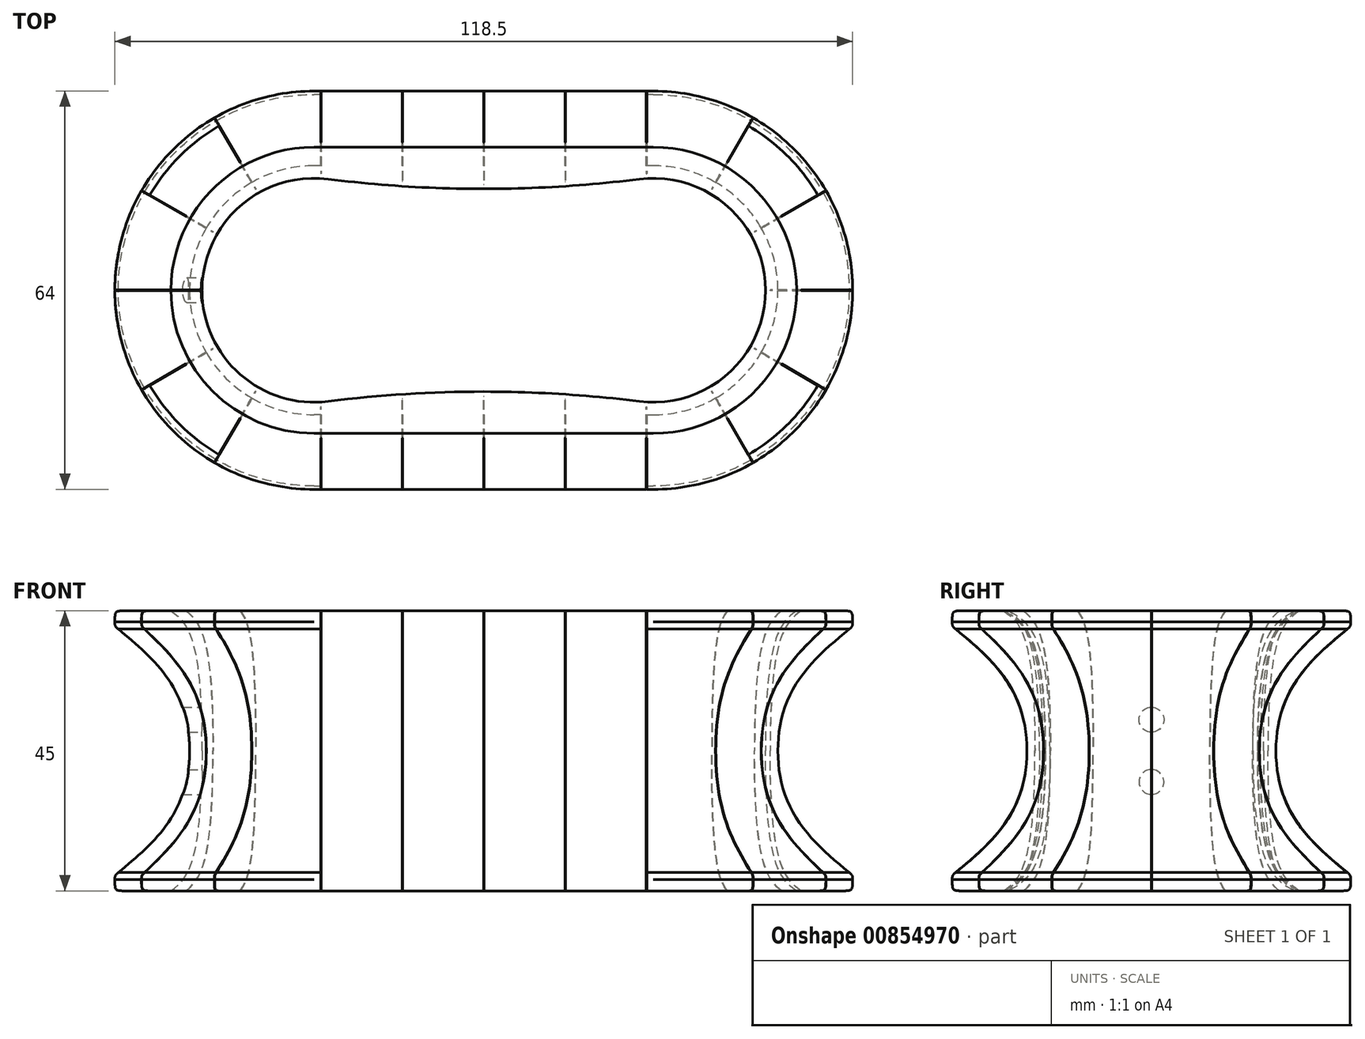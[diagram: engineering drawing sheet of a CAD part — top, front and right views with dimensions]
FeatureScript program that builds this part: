
annotation { "Feature Type Name" : "Feature", "Feature Type Description" : "" }
export const myFeature = defineFeature(function(context is Context, id is Id, definition is map)
    precondition{}
    {
        {
            var Q0;
            Q0=qCreatedBy(makeId("Top.planeOp"),FACE);
            var sketch = newSketch(context, id + "F0", { "sketchPlane" : qUnion([Q0])});
            skArc(sketch, "E0", {"start": v(-25, 17.86) * mm, "mid": v(0, 16.3) * mm, "end": v(25, 17.86) * mm});
            skArc(sketch, "E1", {"start": v(25, -17.86) * mm, "mid": v(45.25, 0) * mm, "end": v(25, 17.86) * mm});
            skArc(sketch, "E2", {"start": v(-25, 17.86) * mm, "mid": v(-45.25, 0) * mm, "end": v(-25, -17.86) * mm});
            skArc(sketch, "E3", {"start": v(25, -17.86) * mm, "mid": v(0, -16.3) * mm, "end": v(-25, -17.86) * mm});
            skLineSegment(sketch, "E4", {"start": v(-27.25, 0) * mm, "end": v(27.25, 0) * mm, "construction": true});
            skSolve(sketch);
        }
        {
            var Q0;
            Q0=qCreatedBy(makeId("Top.planeOp"),FACE);
            cPlane(context, id + "F1", {"entities" : qUnion([Q0]), "cplaneType" : CPlaneType.OFFSET, "offset" : 20 * mm, "width" : 150 * mm, "height" : 150 * mm});
        }
        {
            var Q0;
            Q0=qCreatedBy(makeId("Top.planeOp"),FACE);
            var sketch = newSketch(context, id + "F2", { "sketchPlane" : qUnion([Q0])});
            skArc(sketch, "E5", {"start": v(-27.25, 20) * mm, "mid": v(-47.25, 0) * mm, "end": v(-27.25, -20) * mm});
            skArc(sketch, "E6", {"start": v(27.25, -20) * mm, "mid": v(47.25, 0) * mm, "end": v(27.25, 20) * mm});
            skLineSegment(sketch, "E7", {"start": v(-27.25, 20) * mm, "end": v(27.25, 20) * mm});
            skLineSegment(sketch, "E8", {"start": v(27.25, -20) * mm, "end": v(-27.25, -20) * mm});
            skSolve(sketch);
        }
        {
            var Q0;
            Q0=qCreatedBy(id+"F1.planeOp",FACE);
            var sketch = newSketch(context, id + "F3", { "sketchPlane" : qUnion([Q0])});
            skLineSegment(sketch, "E9.0", {"start": v(-27.25, 32) * mm, "end": v(27.25, 32) * mm});
            skArc(sketch, "E9.1", {"start": v(-27.25, 32) * mm, "mid": v(-59.25, 0) * mm, "end": v(-27.25, -32) * mm});
            skLineSegment(sketch, "E9.2", {"start": v(27.25, -32) * mm, "end": v(-27.25, -32) * mm});
            skArc(sketch, "E9.3", {"start": v(27.25, -32) * mm, "mid": v(59.25, 0) * mm, "end": v(27.25, 32) * mm});
            skSolve(sketch);
        }
        {
            var Q0;
            Q0=makeQuery(id+"F2.imprint","IMPRINT",FACE,{"disambiguationData":[TD([[makeQuery(id+"F2.imprint","IMPRINT",EDGE,{"derivedFrom":sQuery(id+"F2.wireOp",EDGE,"E5")}),1.0]])]});
            var Q1;
            Q1=makeQuery(id+"F3.imprint","IMPRINT",FACE,{"disambiguationData":[TD([[makeQuery(id+"F3.imprint","IMPRINT",EDGE,{"derivedFrom":sQuery(id+"F3.wireOp",EDGE,"E9.0")}),-1.0]])]});
            loft(context, id + "F4", {"startCondition" : LoftEndDerivativeType.NORMAL_TO_PROFILE, "startMagnitude" : 1.5, "sheetProfilesArray" : [{ "sheetProfileEntities" : qUnion([Q0]) }, { "sheetProfileEntities" : qUnion([Q1]) }]});
        }
        {
            var Q0;
            Q0=makeQuery(id+"F4.opLoft","CAP_FACE",FACE,{"disambiguationData":[OSD([makeQuery(id+"F3.imprint","IMPRINT",FACE,{"disambiguationData":[TD([[makeQuery(id+"F3.imprint","IMPRINT",EDGE,{"derivedFrom":sQuery(id+"F3.wireOp",EDGE,"E9.0")}),-1.0]])]})])],"isStart":true});
            extrude(context, id + "F5", {"entities" : qUnion([Q0]), "operationType" : NewBodyOperationType.ADD, "depth" : 2.5 * mm, "offsetDistance" : 25 * mm});
        }
        {
            var Q0;
            Q0=makeQuery(id+"F5.opExtrude","CAP_FACE",FACE,{"disambiguationData":[OSD([makeQuery(id+"F3.imprint","IMPRINT",FACE,{"disambiguationData":[TD([[makeQuery(id+"F3.imprint","IMPRINT",EDGE,{"derivedFrom":sQuery(id+"F3.wireOp",EDGE,"E9.0")}),-1.0]])]})])],"isStart":false});
            var sketch = newSketch(context, id + "F6", { "sketchPlane" : qUnion([Q0])});
            skArc(sketch, "E10", {"start": v(-27.25, 23) * mm, "mid": v(-50.25, 0) * mm, "end": v(-27.25, -23) * mm});
            skArc(sketch, "E11", {"start": v(27.25, -23) * mm, "mid": v(50.25, 0) * mm, "end": v(27.25, 23) * mm});
            skLineSegment(sketch, "E12", {"start": v(-27.25, 23) * mm, "end": v(27.25, 23) * mm});
            skLineSegment(sketch, "E13", {"start": v(27.25, -23) * mm, "end": v(-27.25, -23) * mm});
            skSolve(sketch);
        }
        {
            var Q1;
            Q1=makeQuery(id+"F6.imprint","IMPRINT",FACE,{"disambiguationData":[TD([[makeQuery(id+"F6.imprint","IMPRINT",EDGE,{"derivedFrom":sQuery(id+"F6.wireOp",EDGE,"E10")}),1.0]])]});
            var Q2;
            Q2=makeQuery(id+"F0.imprint","IMPRINT",FACE,{"disambiguationData":[TD([[makeQuery(id+"F0.imprint","IMPRINT",EDGE,{"derivedFrom":sQuery(id+"F0.wireOp",EDGE,"E0")}),-1.0]])]});
            loft(context, id + "F7", {"operationType" : NewBodyOperationType.REMOVE, "endCondition" : LoftEndDerivativeType.NORMAL_TO_PROFILE, "endMagnitude" : 2.5, "sheetProfilesArray" : [{ "sheetProfileEntities" : qUnion([Q1]) }, { "sheetProfileEntities" : qUnion([Q2]) }]});
        }
        {
            var Q0;
            Q0=qCreatedBy(makeId("Top.planeOp"),FACE);
            var sketch = newSketch(context, id + "F8", { "sketchPlane" : qUnion([Q0])});
            skLineSegment(sketch, "E14", {"start": v(-65.05, 0) * mm, "end": v(-65.05, -15.33) * mm, "construction": true});
            skLineSegment(sketch, "E15", {"start": v(-65.05, -15.33) * mm, "end": v(-56.29, -30.51) * mm, "construction": true});
            skLineSegment(sketch, "E16", {"start": v(-56.29, -30.51) * mm, "end": v(-41.1, -39.28) * mm, "construction": true});
            skLineSegment(sketch, "E17", {"start": v(-41.1, -39.28) * mm, "end": v(22.99, -39.28) * mm, "construction": true});
            skSolve(sketch);
        }
        {
            var Q0;
            {var subQ0=sQuery(id+"F3.wireOp",EDGE,"E9.2");var subQ1=sQuery(id+"F3.wireOp",EDGE,"E9.1");var subQ2=sQuery(id+"F3.wireOp",EDGE,"E9.0");Q0=makeQuery(id+"F5.boolean.opBoolean","MERGE",EDGE,{"derivedFrom":[makeQuery(id+"F4.opLoft","MID_CAP_EDGE",EDGE,{"disambiguationData":[OSD([subQ2,subQ1,subQ0])],"capPos":1.0}),makeQuery(id+"F5.opExtrude","CAP_EDGE",EDGE,{"disambiguationData":[OSD([subQ2,subQ1,subQ0])],"isStart":true})]});}
            var Q1;
            Q1=makeQuery(id+"F5.opExtrude","CAP_EDGE",EDGE,{"disambiguationData":[OSD([sQuery(id+"F3.wireOp",EDGE,"E9.0"),sQuery(id+"F3.wireOp",EDGE,"E9.1"),sQuery(id+"F3.wireOp",EDGE,"E9.2")])],"isStart":false});
            fillet(context, id + "F9", {"entities" : qUnion([Q0, Q1]), "radius" : 1.5 * mm, "tangentPropagation" : true, "rho" : .7, "crossSection" : FilletCrossSection.CONIC, "allowEdgeOverflow" : false});
        }
        {
            var Q0;
            Q0=sQuery(id+"F8.wireOp",EDGE,"E14");
            cPlane(context, id + "F10", {"entities" : qUnion([Q0]), "cplaneType" : CPlaneType.LINE_ANGLE, "offset" : 25 * mm, "angle" : 90 * degree, "width" : 150 * mm, "height" : 150 * mm});
        }
        {
            var Q0;
            Q0=sQuery(id+"F8.wireOp",EDGE,"E15");
            cPlane(context, id + "F11", {"entities" : qUnion([Q0]), "cplaneType" : CPlaneType.LINE_ANGLE, "offset" : 25 * mm, "angle" : 90 * degree, "width" : 150 * mm, "height" : 150 * mm});
        }
        {
            var Q0;
            Q0=sQuery(id+"F8.wireOp",EDGE,"E16");
            cPlane(context, id + "F12", {"entities" : qUnion([Q0]), "cplaneType" : CPlaneType.LINE_ANGLE, "offset" : 90 * mm, "angle" : 0 * degree, "width" : 150 * mm, "height" : 150 * mm});
        }
        {
            var Q0;
            Q0=sQuery(id+"F8.wireOp",EDGE,"E17");
            cPlane(context, id + "F13", {"entities" : qUnion([Q0]), "cplaneType" : CPlaneType.LINE_ANGLE, "offset" : 25 * mm, "angle" : 0 * degree, "oppositeDirection" : true, "width" : 150 * mm, "height" : 150 * mm});
        }
        {
            var Q0;
            Q0=qCreatedBy(id+"F10.planeOp",FACE);
            var sketch = newSketch(context, id + "F14", { "sketchPlane" : qUnion([Q0])});
            skLineSegment(sketch, "E18.bottom", {"start": v(0.04, 0) * mm, "end": v(-0.04, 0) * mm});
            skLineSegment(sketch, "E18.top", {"start": v(0.04, 22.5) * mm, "end": v(-0.04, 22.5) * mm});
            skLineSegment(sketch, "E18.left", {"start": v(0.04, 0) * mm, "end": v(0.04, 22.5) * mm});
            skLineSegment(sketch, "E18.right", {"start": v(-0.04, 0) * mm, "end": v(-0.04, 22.5) * mm});
            skSolve(sketch);
        }
        {
            var Q0;
            Q0=qCreatedBy(id+"F11.planeOp",FACE);
            var sketch = newSketch(context, id + "F15", { "sketchPlane" : qUnion([Q0])});
            skLineSegment(sketch, "E19.bottom", {"start": v(13.66, 0) * mm, "end": v(13.59, 0) * mm});
            skLineSegment(sketch, "E19.top", {"start": v(13.66, 22.5) * mm, "end": v(13.59, 22.5) * mm});
            skLineSegment(sketch, "E19.left", {"start": v(13.66, 0) * mm, "end": v(13.66, 22.5) * mm});
            skLineSegment(sketch, "E19.right", {"start": v(13.59, 0) * mm, "end": v(13.59, 22.5) * mm});
            skSolve(sketch);
        }
        {
            var Q0;
            Q0=qCreatedBy(id+"F12.planeOp",FACE);
            var sketch = newSketch(context, id + "F16", { "sketchPlane" : qUnion([Q0])});
            skLineSegment(sketch, "E20.bottom", {"start": v(23.64, 0) * mm, "end": v(23.56, 0) * mm});
            skLineSegment(sketch, "E20.top", {"start": v(23.64, 22.5) * mm, "end": v(23.56, 22.5) * mm});
            skLineSegment(sketch, "E20.left", {"start": v(23.56, 0) * mm, "end": v(23.56, 22.5) * mm});
            skLineSegment(sketch, "E20.right", {"start": v(23.64, 0) * mm, "end": v(23.64, 22.5) * mm});
            skSolve(sketch);
        }
        {
            var Q0;
            Q0=qCreatedBy(id+"F13.planeOp",FACE);
            var sketch = newSketch(context, id + "F17", { "sketchPlane" : qUnion([Q0])});
            skLineSegment(sketch, "E21.bottom", {"start": v(0.04, 0) * mm, "end": v(-0.04, 0) * mm});
            skLineSegment(sketch, "E21.top", {"start": v(0.04, 22.5) * mm, "end": v(-0.04, 22.5) * mm});
            skLineSegment(sketch, "E21.left", {"start": v(0.04, 0) * mm, "end": v(0.04, 22.5) * mm});
            skLineSegment(sketch, "E21.right", {"start": v(-0.04, 0) * mm, "end": v(-0.04, 22.5) * mm});
            skLineSegment(sketch, "E22.bottom", {"start": v(13.04, 0) * mm, "end": v(13.11, 0) * mm});
            skLineSegment(sketch, "E22.top", {"start": v(13.04, 22.5) * mm, "end": v(13.11, 22.5) * mm});
            skLineSegment(sketch, "E22.left", {"start": v(13.04, 0) * mm, "end": v(13.04, 22.5) * mm});
            skLineSegment(sketch, "E22.right", {"start": v(13.11, 0) * mm, "end": v(13.11, 22.5) * mm});
            skLineSegment(sketch, "E23.bottom", {"start": v(26.11, 0) * mm, "end": v(26.19, 0) * mm});
            skLineSegment(sketch, "E23.top", {"start": v(26.11, 22.5) * mm, "end": v(26.19, 22.5) * mm});
            skLineSegment(sketch, "E23.left", {"start": v(26.11, 0) * mm, "end": v(26.11, 22.5) * mm});
            skLineSegment(sketch, "E23.right", {"start": v(26.19, 0) * mm, "end": v(26.19, 22.5) * mm});
            skLineSegment(sketch, "E24", {"start": v(26.11, 11.25) * mm, "end": v(13.11, 11.25) * mm, "construction": true});
            skLineSegment(sketch, "E25", {"start": v(13.04, 11.25) * mm, "end": v(0.04, 11.25) * mm, "construction": true});
            skSolve(sketch);
        }
        {
            var Q0;
            Q0=qSketchRegion(id+"F14",true);
            var Q1;
            Q1=makeQuery(id+"F7.boolean.opBoolean","COPY",FACE,{"derivedFrom":makeQuery(id+"F7.opLoft","SWEPT_FACE",FACE,{"disambiguationData":[OSD([sQuery(id+"F0.wireOp",EDGE,"E0"),sQuery(id+"F0.wireOp",EDGE,"E1"),sQuery(id+"F0.wireOp",EDGE,"E2"),sQuery(id+"F6.wireOp",EDGE,"E10"),sQuery(id+"F6.wireOp",EDGE,"E11"),sQuery(id+"F6.wireOp",EDGE,"E12")])]})});
            extrude(context, id + "F18", {"entities" : qUnion([Q0]), "operationType" : NewBodyOperationType.REMOVE, "endBound" : BoundingType.UP_TO_SURFACE, "depth" : 25 * mm, "endBoundEntityFace" : qUnion([Q1]), "hasOffset" : true, "offsetDistance" : .75 * mm});
        }
        {
            var Q0;
            Q0=makeQuery(id+"F15.imprint","IMPRINT",FACE,{"disambiguationData":[TD([[makeQuery(id+"F15.imprint","IMPRINT",EDGE,{"derivedFrom":sQuery(id+"F15.wireOp",EDGE,"E19.bottom")}),-1.0]])]});
            var Q1;
            Q1=makeQuery(id+"F7.boolean.opBoolean","COPY",FACE,{"derivedFrom":makeQuery(id+"F7.opLoft","SWEPT_FACE",FACE,{"disambiguationData":[OSD([sQuery(id+"F0.wireOp",EDGE,"E0"),sQuery(id+"F0.wireOp",EDGE,"E1"),sQuery(id+"F0.wireOp",EDGE,"E2"),sQuery(id+"F6.wireOp",EDGE,"E10"),sQuery(id+"F6.wireOp",EDGE,"E11"),sQuery(id+"F6.wireOp",EDGE,"E12")])]})});
            extrude(context, id + "F19", {"entities" : qUnion([Q0]), "operationType" : NewBodyOperationType.REMOVE, "endBound" : BoundingType.UP_TO_SURFACE, "depth" : 25 * mm, "endBoundEntityFace" : qUnion([Q1]), "hasOffset" : true, "offsetDistance" : .75 * mm});
        }
        {
            var Q0;
            Q0=makeQuery(id+"F16.imprint","IMPRINT",FACE,{"disambiguationData":[TD([[makeQuery(id+"F16.imprint","IMPRINT",EDGE,{"derivedFrom":sQuery(id+"F16.wireOp",EDGE,"E20.bottom")}),-1.0]])]});
            var Q1;
            Q1=qConstructionFilter(qBodyType(qCreatedBy(id+"F16",EDGE),BodyType.WIRE),ConstructionObject.NO);
            var Q2;
            Q2=makeQuery(id+"F7.boolean.opBoolean","COPY",FACE,{"derivedFrom":makeQuery(id+"F7.opLoft","SWEPT_FACE",FACE,{"disambiguationData":[OSD([sQuery(id+"F0.wireOp",EDGE,"E0"),sQuery(id+"F0.wireOp",EDGE,"E1"),sQuery(id+"F0.wireOp",EDGE,"E2"),sQuery(id+"F6.wireOp",EDGE,"E10"),sQuery(id+"F6.wireOp",EDGE,"E11"),sQuery(id+"F6.wireOp",EDGE,"E12")])]})});
            extrude(context, id + "F20", {"entities" : qUnion([Q0]), "operationType" : NewBodyOperationType.REMOVE, "surfaceEntities" : qUnion([Q1]), "endBound" : BoundingType.UP_TO_SURFACE, "depth" : 25 * mm, "endBoundEntityFace" : qUnion([Q2]), "hasOffset" : true, "offsetDistance" : .75 * mm});
        }
        {
            var Q0;
            Q0=qSketchRegion(id+"F17",true);
            var Q1;
            Q1=makeQuery(id+"F7.boolean.opBoolean","COPY",FACE,{"derivedFrom":makeQuery(id+"F7.opLoft","SWEPT_FACE",FACE,{"disambiguationData":[OSD([sQuery(id+"F0.wireOp",EDGE,"E0"),sQuery(id+"F0.wireOp",EDGE,"E1"),sQuery(id+"F0.wireOp",EDGE,"E2"),sQuery(id+"F6.wireOp",EDGE,"E10"),sQuery(id+"F6.wireOp",EDGE,"E11"),sQuery(id+"F6.wireOp",EDGE,"E12")])]})});
            extrude(context, id + "F21", {"entities" : qUnion([Q0]), "operationType" : NewBodyOperationType.REMOVE, "endBound" : BoundingType.UP_TO_SURFACE, "depth" : 25 * mm, "endBoundEntityFace" : qUnion([Q1]), "hasOffset" : true, "offsetDistance" : .75 * mm});
        }
        {
            var Q0;
            Q0=qCreatedBy(makeId("Top.planeOp"),FACE);
            var sketch = newSketch(context, id + "F22", { "sketchPlane" : qUnion([Q0])});
            skLineSegment(sketch, "E26", {"start": v(0, 0) * mm, "end": v(0, -60) * mm});
            skLineSegment(sketch, "E27", {"start": v(0, -60) * mm, "end": v(120, -60) * mm});
            skLineSegment(sketch, "E28", {"start": v(120, -60) * mm, "end": v(120, 60) * mm});
            skLineSegment(sketch, "E29", {"start": v(120, 60) * mm, "end": v(-120, 60) * mm});
            skLineSegment(sketch, "E30", {"start": v(-120, 60) * mm, "end": v(-120, 0) * mm});
            skLineSegment(sketch, "E31", {"start": v(-120, 0) * mm, "end": v(0, 0) * mm});
            skSolve(sketch);
        }
        {
            var Q0;
            Q0=qSketchRegion(id+"F22",true);
            extrude(context, id + "F23", {"entities" : qUnion([Q0]), "operationType" : NewBodyOperationType.REMOVE, "endBound" : BoundingType.THROUGH_ALL, "depth" : 25 * mm, "offsetDistance" : 25 * mm});
        }
        {
            var Q0;
            Q0=makeQuery(id+"F4.opLoft","SWEPT_BODY",BODY,{"disambiguationData":[OSD([makeQuery(id+"F2.imprint","IMPRINT",FACE,{"disambiguationData":[TD([[makeQuery(id+"F2.imprint","IMPRINT",EDGE,{"derivedFrom":sQuery(id+"F2.wireOp",EDGE,"E5")}),1.0]])]}),makeQuery(id+"F3.imprint","IMPRINT",FACE,{"disambiguationData":[TD([[makeQuery(id+"F3.imprint","IMPRINT",EDGE,{"derivedFrom":sQuery(id+"F3.wireOp",EDGE,"E9.0")}),-1.0]])]})])]});
            var Q1;
            Q1=makeQuery(id+"F23.boolean.opBoolean","COPY",FACE,{"derivedFrom":makeQuery(id+"F23.opExtrude","SWEPT_FACE",FACE,{"disambiguationData":[OSD([sQuery(id+"F22.wireOp",EDGE,"E26")])]})});
            mirror(context, id + "F24", {"operationType" : NewBodyOperationType.ADD, "entities" : qUnion([Q0]), "mirrorPlane" : qUnion([Q1])});
        }
        {
            var Q0;
            Q0=makeQuery(id+"F4.opLoft","SWEPT_BODY",BODY,{"disambiguationData":[OSD([makeQuery(id+"F2.imprint","IMPRINT",FACE,{"disambiguationData":[TD([[makeQuery(id+"F2.imprint","IMPRINT",EDGE,{"derivedFrom":sQuery(id+"F2.wireOp",EDGE,"E5")}),1.0]])]}),makeQuery(id+"F3.imprint","IMPRINT",FACE,{"disambiguationData":[TD([[makeQuery(id+"F3.imprint","IMPRINT",EDGE,{"derivedFrom":sQuery(id+"F3.wireOp",EDGE,"E9.0")}),-1.0]])]})])]});
            var Q1;
            Q1=makeQuery(id+"F24.opPattern","COPY",FACE,{"derivedFrom":makeQuery(id+"F23.boolean.opBoolean","COPY",FACE,{"derivedFrom":makeQuery(id+"F23.opExtrude","SWEPT_FACE",FACE,{"disambiguationData":[OSD([sQuery(id+"F22.wireOp",EDGE,"E31")])]})}),"instanceName":"1"});
            mirror(context, id + "F25", {"operationType" : NewBodyOperationType.ADD, "entities" : qUnion([Q0]), "mirrorPlane" : qUnion([Q1])});
        }
        {
            var Q0;
            Q0=qCreatedBy(makeId("Right.planeOp"),FACE);
            var sketch = newSketch(context, id + "F26", { "sketchPlane" : qUnion([Q0])});
            skLineSegment(sketch, "E32.bottom", {"start": v(0.04, 0) * mm, "end": v(-0.04, 0) * mm});
            skLineSegment(sketch, "E32.top", {"start": v(0.04, 22.5) * mm, "end": v(-0.04, 22.5) * mm});
            skLineSegment(sketch, "E32.left", {"start": v(0.04, 0) * mm, "end": v(0.04, 22.5) * mm});
            skLineSegment(sketch, "E32.right", {"start": v(-0.04, 0) * mm, "end": v(-0.04, 22.5) * mm});
            skCircle(sketch, "E33", {"center": v(0, 5) * mm, "radius": 2 * mm});
            skSolve(sketch);
        }
        {
            var Q0;
            Q0=qSketchRegion(id+"F26",true);
            extrude(context, id + "F27", {"entities" : qUnion([Q0]), "operationType" : NewBodyOperationType.REMOVE, "endBound" : BoundingType.THROUGH_ALL, "oppositeDirection" : true, "depth" : 25 * mm, "offsetDistance" : 25 * mm});
        }
        {
            var Q0;
            Q0=makeQuery(id+"F4.opLoft","SWEPT_BODY",BODY,{"disambiguationData":[OSD([makeQuery(id+"F2.imprint","IMPRINT",FACE,{"disambiguationData":[TD([[makeQuery(id+"F2.imprint","IMPRINT",EDGE,{"derivedFrom":sQuery(id+"F2.wireOp",EDGE,"E5")}),1.0]])]}),makeQuery(id+"F3.imprint","IMPRINT",FACE,{"disambiguationData":[TD([[makeQuery(id+"F3.imprint","IMPRINT",EDGE,{"derivedFrom":sQuery(id+"F3.wireOp",EDGE,"E9.0")}),-1.0]])]})])]});
            var Q1;
            {var subQ0=makeQuery(id+"F4.opLoft","CAP_FACE",FACE,{"disambiguationData":[OSD([makeQuery(id+"F2.imprint","IMPRINT",FACE,{"disambiguationData":[TD([[makeQuery(id+"F2.imprint","IMPRINT",EDGE,{"derivedFrom":sQuery(id+"F2.wireOp",EDGE,"E5")}),1.0]])]})])],"isStart":true});var subQ1=makeQuery(id+"F24.boolean.opBoolean","MERGE",FACE,{"derivedFrom":[subQ0,makeQuery(id+"F24.opPattern","COPY",FACE,{"derivedFrom":subQ0,"instanceName":"1"})]});Q1=makeQuery(id+"F25.boolean.opBoolean","MERGE",FACE,{"derivedFrom":[subQ1,makeQuery(id+"F25.opPattern","COPY",FACE,{"derivedFrom":subQ1,"instanceName":"1"})]});}
            mirror(context, id + "F28", {"operationType" : NewBodyOperationType.ADD, "entities" : qUnion([Q0]), "mirrorPlane" : qUnion([Q1])});
        }
    });
